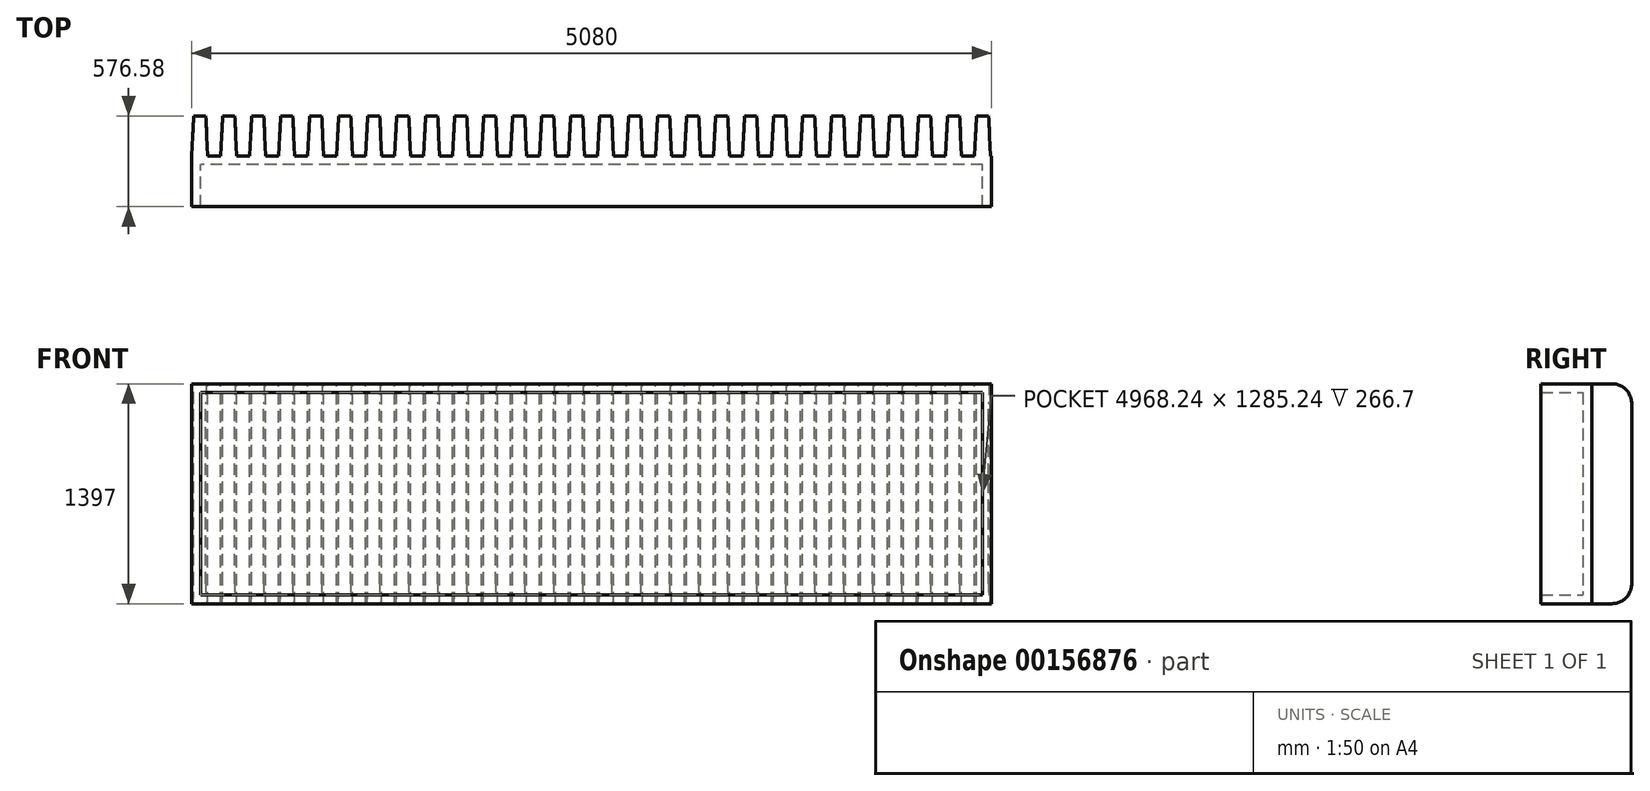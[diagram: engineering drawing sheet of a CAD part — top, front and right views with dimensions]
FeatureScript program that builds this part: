
annotation { "Feature Type Name" : "Feature", "Feature Type Description" : "" }
export const myFeature = defineFeature(function(context is Context, id is Id, definition is map)
    precondition{}
    {
        {
            var Q0;
            Q0=qCreatedBy(makeId("Front.planeOp"),FACE);
            var sketch = newSketch(context, id + "F0", { "sketchPlane" : qUnion([Q0])});
            skLineSegment(sketch, "E0.bottom", {"start": v(2540, 698.5) * mm, "end": v(-2540, 698.5) * mm});
            skLineSegment(sketch, "E0.top", {"start": v(2540, -698.5) * mm, "end": v(-2540, -698.5) * mm});
            skLineSegment(sketch, "E0.left", {"start": v(2540, 698.5) * mm, "end": v(2540, -698.5) * mm});
            skLineSegment(sketch, "E0.right", {"start": v(-2540, 698.5) * mm, "end": v(-2540, -698.5) * mm});
            skPoint(sketch, "E0.middle", {"position": v(0, 0) * mm});
            skSolve(sketch);
        }
        {
            var Q0;
            Q0 = qSketchRegion(id + "F0", true);
            extrude(context, id + "F1", {"entities" : qUnion([Q0]), "depth" : 322.58 * mm});
        }
        {
            var Q0;
            Q0=makeQuery(id+"F1.opExtrude","SWEPT_FACE",FACE,{"disambiguationData":[OSD([sQuery(id+"F0.wireOp",EDGE,"E0.bottom")])]});
            var sketch = newSketch(context, id + "F2", { "sketchPlane" : qUnion([Q0])});
            skLineSegment(sketch, "E1", {"start": v(-2540, 0) * mm, "end": v(-2526.69, 254) * mm});
            skLineSegment(sketch, "E2", {"start": v(-2526.69, 254) * mm, "end": v(-2450.49, 254) * mm});
            skLineSegment(sketch, "E3", {"start": v(-2450.49, 254) * mm, "end": v(-2437.18, 0) * mm});
            skLineSegment(sketch, "E4", {"start": v(-2437.18, 0) * mm, "end": v(-2540, 0) * mm});
            skLineSegment(sketch, "E5.1.0.0", {"start": v(-2266.34, 254) * mm, "end": v(-2253.03, 0) * mm});
            skLineSegment(sketch, "E5.1.0.1", {"start": v(-2342.54, 254) * mm, "end": v(-2266.34, 254) * mm});
            skLineSegment(sketch, "E5.1.0.2", {"start": v(-2355.85, 0) * mm, "end": v(-2342.54, 254) * mm});
            skLineSegment(sketch, "E5.1.0.3", {"start": v(-2253.03, 0) * mm, "end": v(-2355.85, 0) * mm});
            skLineSegment(sketch, "E5.2.0.0", {"start": v(-2082.19, 254) * mm, "end": v(-2068.88, 0) * mm});
            skLineSegment(sketch, "E5.2.0.1", {"start": v(-2158.39, 254) * mm, "end": v(-2082.19, 254) * mm});
            skLineSegment(sketch, "E5.2.0.2", {"start": v(-2171.7, 0) * mm, "end": v(-2158.39, 254) * mm});
            skLineSegment(sketch, "E5.2.0.3", {"start": v(-2068.88, 0) * mm, "end": v(-2171.7, 0) * mm});
            skLineSegment(sketch, "E5.3.0.0", {"start": v(-1898.04, 254) * mm, "end": v(-1884.73, 0) * mm});
            skLineSegment(sketch, "E5.3.0.1", {"start": v(-1974.24, 254) * mm, "end": v(-1898.04, 254) * mm});
            skLineSegment(sketch, "E5.3.0.2", {"start": v(-1987.55, 0) * mm, "end": v(-1974.24, 254) * mm});
            skLineSegment(sketch, "E5.3.0.3", {"start": v(-1884.73, 0) * mm, "end": v(-1987.55, 0) * mm});
            skLineSegment(sketch, "E5.4.0.0", {"start": v(-1713.89, 254) * mm, "end": v(-1700.58, 0) * mm});
            skLineSegment(sketch, "E5.4.0.1", {"start": v(-1790.09, 254) * mm, "end": v(-1713.89, 254) * mm});
            skLineSegment(sketch, "E5.4.0.2", {"start": v(-1803.4, 0) * mm, "end": v(-1790.09, 254) * mm});
            skLineSegment(sketch, "E5.4.0.3", {"start": v(-1700.58, 0) * mm, "end": v(-1803.4, 0) * mm});
            skLineSegment(sketch, "E5.5.0.0", {"start": v(-1529.74, 254) * mm, "end": v(-1516.43, 0) * mm});
            skLineSegment(sketch, "E5.5.0.1", {"start": v(-1605.94, 254) * mm, "end": v(-1529.74, 254) * mm});
            skLineSegment(sketch, "E5.5.0.2", {"start": v(-1619.25, 0) * mm, "end": v(-1605.94, 254) * mm});
            skLineSegment(sketch, "E5.5.0.3", {"start": v(-1516.43, 0) * mm, "end": v(-1619.25, 0) * mm});
            skLineSegment(sketch, "E5.6.0.0", {"start": v(-1345.59, 254) * mm, "end": v(-1332.28, 0) * mm});
            skLineSegment(sketch, "E5.6.0.1", {"start": v(-1421.79, 254) * mm, "end": v(-1345.59, 254) * mm});
            skLineSegment(sketch, "E5.6.0.2", {"start": v(-1435.1, 0) * mm, "end": v(-1421.79, 254) * mm});
            skLineSegment(sketch, "E5.6.0.3", {"start": v(-1332.28, 0) * mm, "end": v(-1435.1, 0) * mm});
            skLineSegment(sketch, "E5.7.0.0", {"start": v(-1161.44, 254) * mm, "end": v(-1148.13, 0) * mm});
            skLineSegment(sketch, "E5.7.0.1", {"start": v(-1237.64, 254) * mm, "end": v(-1161.44, 254) * mm});
            skLineSegment(sketch, "E5.7.0.2", {"start": v(-1250.95, 0) * mm, "end": v(-1237.64, 254) * mm});
            skLineSegment(sketch, "E5.7.0.3", {"start": v(-1148.13, 0) * mm, "end": v(-1250.95, 0) * mm});
            skLineSegment(sketch, "E5.8.0.0", {"start": v(-977.29, 254) * mm, "end": v(-963.98, 0) * mm});
            skLineSegment(sketch, "E5.8.0.1", {"start": v(-1053.49, 254) * mm, "end": v(-977.29, 254) * mm});
            skLineSegment(sketch, "E5.8.0.2", {"start": v(-1066.8, 0) * mm, "end": v(-1053.49, 254) * mm});
            skLineSegment(sketch, "E5.8.0.3", {"start": v(-963.98, 0) * mm, "end": v(-1066.8, 0) * mm});
            skLineSegment(sketch, "E5.9.0.0", {"start": v(-793.14, 254) * mm, "end": v(-779.83, 0) * mm});
            skLineSegment(sketch, "E5.9.0.1", {"start": v(-869.34, 254) * mm, "end": v(-793.14, 254) * mm});
            skLineSegment(sketch, "E5.9.0.2", {"start": v(-882.65, 0) * mm, "end": v(-869.34, 254) * mm});
            skLineSegment(sketch, "E5.9.0.3", {"start": v(-779.83, 0) * mm, "end": v(-882.65, 0) * mm});
            skLineSegment(sketch, "E5.10.0.0", {"start": v(-608.99, 254) * mm, "end": v(-595.68, 0) * mm});
            skLineSegment(sketch, "E5.10.0.1", {"start": v(-685.19, 254) * mm, "end": v(-608.99, 254) * mm});
            skLineSegment(sketch, "E5.10.0.2", {"start": v(-698.5, 0) * mm, "end": v(-685.19, 254) * mm});
            skLineSegment(sketch, "E5.10.0.3", {"start": v(-595.68, 0) * mm, "end": v(-698.5, 0) * mm});
            skLineSegment(sketch, "E5.11.0.0", {"start": v(-424.84, 254) * mm, "end": v(-411.53, 0) * mm});
            skLineSegment(sketch, "E5.11.0.1", {"start": v(-501.04, 254) * mm, "end": v(-424.84, 254) * mm});
            skLineSegment(sketch, "E5.11.0.2", {"start": v(-514.35, 0) * mm, "end": v(-501.04, 254) * mm});
            skLineSegment(sketch, "E5.11.0.3", {"start": v(-411.53, 0) * mm, "end": v(-514.35, 0) * mm});
            skLineSegment(sketch, "E5.12.0.0", {"start": v(-240.69, 254) * mm, "end": v(-227.38, 0) * mm});
            skLineSegment(sketch, "E5.12.0.1", {"start": v(-316.89, 254) * mm, "end": v(-240.69, 254) * mm});
            skLineSegment(sketch, "E5.12.0.2", {"start": v(-330.2, 0) * mm, "end": v(-316.89, 254) * mm});
            skLineSegment(sketch, "E5.12.0.3", {"start": v(-227.38, 0) * mm, "end": v(-330.2, 0) * mm});
            skLineSegment(sketch, "E5.13.0.0", {"start": v(-56.54, 254) * mm, "end": v(-43.23, 0) * mm});
            skLineSegment(sketch, "E5.13.0.1", {"start": v(-132.74, 254) * mm, "end": v(-56.54, 254) * mm});
            skLineSegment(sketch, "E5.13.0.2", {"start": v(-146.05, 0) * mm, "end": v(-132.74, 254) * mm});
            skLineSegment(sketch, "E5.13.0.3", {"start": v(-43.23, 0) * mm, "end": v(-146.05, 0) * mm});
            skLineSegment(sketch, "E5.14.0.0", {"start": v(127.61, 254) * mm, "end": v(140.92, 0) * mm});
            skLineSegment(sketch, "E5.14.0.1", {"start": v(51.41, 254) * mm, "end": v(127.61, 254) * mm});
            skLineSegment(sketch, "E5.14.0.2", {"start": v(38.1, 0) * mm, "end": v(51.41, 254) * mm});
            skLineSegment(sketch, "E5.14.0.3", {"start": v(140.92, 0) * mm, "end": v(38.1, 0) * mm});
            skLineSegment(sketch, "E5.15.0.0", {"start": v(311.76, 254) * mm, "end": v(325.07, 0) * mm});
            skLineSegment(sketch, "E5.15.0.1", {"start": v(235.56, 254) * mm, "end": v(311.76, 254) * mm});
            skLineSegment(sketch, "E5.15.0.2", {"start": v(222.25, 0) * mm, "end": v(235.56, 254) * mm});
            skLineSegment(sketch, "E5.15.0.3", {"start": v(325.07, 0) * mm, "end": v(222.25, 0) * mm});
            skLineSegment(sketch, "E5.16.0.0", {"start": v(495.91, 254) * mm, "end": v(509.22, 0) * mm});
            skLineSegment(sketch, "E5.16.0.1", {"start": v(419.71, 254) * mm, "end": v(495.91, 254) * mm});
            skLineSegment(sketch, "E5.16.0.2", {"start": v(406.4, 0) * mm, "end": v(419.71, 254) * mm});
            skLineSegment(sketch, "E5.16.0.3", {"start": v(509.22, 0) * mm, "end": v(406.4, 0) * mm});
            skLineSegment(sketch, "E5.17.0.0", {"start": v(680.06, 254) * mm, "end": v(693.37, 0) * mm});
            skLineSegment(sketch, "E5.17.0.1", {"start": v(603.86, 254) * mm, "end": v(680.06, 254) * mm});
            skLineSegment(sketch, "E5.17.0.2", {"start": v(590.55, 0) * mm, "end": v(603.86, 254) * mm});
            skLineSegment(sketch, "E5.17.0.3", {"start": v(693.37, 0) * mm, "end": v(590.55, 0) * mm});
            skLineSegment(sketch, "E5.18.0.0", {"start": v(864.21, 254) * mm, "end": v(877.52, 0) * mm});
            skLineSegment(sketch, "E5.18.0.1", {"start": v(788.01, 254) * mm, "end": v(864.21, 254) * mm});
            skLineSegment(sketch, "E5.18.0.2", {"start": v(774.7, 0) * mm, "end": v(788.01, 254) * mm});
            skLineSegment(sketch, "E5.18.0.3", {"start": v(877.52, 0) * mm, "end": v(774.7, 0) * mm});
            skLineSegment(sketch, "E5.19.0.0", {"start": v(1048.36, 254) * mm, "end": v(1061.67, 0) * mm});
            skLineSegment(sketch, "E5.19.0.1", {"start": v(972.16, 254) * mm, "end": v(1048.36, 254) * mm});
            skLineSegment(sketch, "E5.19.0.2", {"start": v(958.85, 0) * mm, "end": v(972.16, 254) * mm});
            skLineSegment(sketch, "E5.19.0.3", {"start": v(1061.67, 0) * mm, "end": v(958.85, 0) * mm});
            skLineSegment(sketch, "E5.20.0.0", {"start": v(1232.51, 254) * mm, "end": v(1245.82, 0) * mm});
            skLineSegment(sketch, "E5.20.0.1", {"start": v(1156.31, 254) * mm, "end": v(1232.51, 254) * mm});
            skLineSegment(sketch, "E5.20.0.2", {"start": v(1143, 0) * mm, "end": v(1156.31, 254) * mm});
            skLineSegment(sketch, "E5.20.0.3", {"start": v(1245.82, 0) * mm, "end": v(1143, 0) * mm});
            skLineSegment(sketch, "E5.21.0.0", {"start": v(1416.66, 254) * mm, "end": v(1429.97, 0) * mm});
            skLineSegment(sketch, "E5.21.0.1", {"start": v(1340.46, 254) * mm, "end": v(1416.66, 254) * mm});
            skLineSegment(sketch, "E5.21.0.2", {"start": v(1327.15, 0) * mm, "end": v(1340.46, 254) * mm});
            skLineSegment(sketch, "E5.21.0.3", {"start": v(1429.97, 0) * mm, "end": v(1327.15, 0) * mm});
            skLineSegment(sketch, "E5.22.0.0", {"start": v(1600.81, 254) * mm, "end": v(1614.12, 0) * mm});
            skLineSegment(sketch, "E5.22.0.1", {"start": v(1524.61, 254) * mm, "end": v(1600.81, 254) * mm});
            skLineSegment(sketch, "E5.22.0.2", {"start": v(1511.3, 0) * mm, "end": v(1524.61, 254) * mm});
            skLineSegment(sketch, "E5.22.0.3", {"start": v(1614.12, 0) * mm, "end": v(1511.3, 0) * mm});
            skLineSegment(sketch, "E5.23.0.0", {"start": v(1784.96, 254) * mm, "end": v(1798.27, 0) * mm});
            skLineSegment(sketch, "E5.23.0.1", {"start": v(1708.76, 254) * mm, "end": v(1784.96, 254) * mm});
            skLineSegment(sketch, "E5.23.0.2", {"start": v(1695.45, 0) * mm, "end": v(1708.76, 254) * mm});
            skLineSegment(sketch, "E5.23.0.3", {"start": v(1798.27, 0) * mm, "end": v(1695.45, 0) * mm});
            skLineSegment(sketch, "E5.24.0.0", {"start": v(1969.11, 254) * mm, "end": v(1982.42, 0) * mm});
            skLineSegment(sketch, "E5.24.0.1", {"start": v(1892.91, 254) * mm, "end": v(1969.11, 254) * mm});
            skLineSegment(sketch, "E5.24.0.2", {"start": v(1879.6, 0) * mm, "end": v(1892.91, 254) * mm});
            skLineSegment(sketch, "E5.24.0.3", {"start": v(1982.42, 0) * mm, "end": v(1879.6, 0) * mm});
            skLineSegment(sketch, "E5.25.0.0", {"start": v(2153.26, 254) * mm, "end": v(2166.57, 0) * mm});
            skLineSegment(sketch, "E5.25.0.1", {"start": v(2077.06, 254) * mm, "end": v(2153.26, 254) * mm});
            skLineSegment(sketch, "E5.25.0.2", {"start": v(2063.75, 0) * mm, "end": v(2077.06, 254) * mm});
            skLineSegment(sketch, "E5.25.0.3", {"start": v(2166.57, 0) * mm, "end": v(2063.75, 0) * mm});
            skLineSegment(sketch, "E5.26.0.0", {"start": v(2337.41, 254) * mm, "end": v(2350.72, 0) * mm});
            skLineSegment(sketch, "E5.26.0.1", {"start": v(2261.21, 254) * mm, "end": v(2337.41, 254) * mm});
            skLineSegment(sketch, "E5.26.0.2", {"start": v(2247.9, 0) * mm, "end": v(2261.21, 254) * mm});
            skLineSegment(sketch, "E5.26.0.3", {"start": v(2350.72, 0) * mm, "end": v(2247.9, 0) * mm});
            skLineSegment(sketch, "E5.27.0.0", {"start": v(2521.56, 254) * mm, "end": v(2534.87, 0) * mm});
            skLineSegment(sketch, "E5.27.0.1", {"start": v(2445.36, 254) * mm, "end": v(2521.56, 254) * mm});
            skLineSegment(sketch, "E5.27.0.2", {"start": v(2432.05, 0) * mm, "end": v(2445.36, 254) * mm});
            skLineSegment(sketch, "E5.27.0.3", {"start": v(2534.87, 0) * mm, "end": v(2432.05, 0) * mm});
            skLineSegment(sketch, "E5.direction1", {"start": v(-2437.18, 0) * mm, "end": v(-2253.03, 0) * mm, "construction": true});
            skSolve(sketch);
        }
        {
            var Q0;
            Q0 = qSketchRegion(id + "F2", true);
            extrude(context, id + "F3", {"entities" : qUnion([Q0]), "operationType" : NewBodyOperationType.ADD, "oppositeDirection" : true, "depth" : 1397 * mm});
        }
        {
            var Q0;
            Q0=makeQuery(id+"F1.opExtrude","CAP_FACE",FACE,{"disambiguationData":[OSD([sQuery(id+"F0.wireOp",EDGE,"E0.bottom"),sQuery(id+"F0.wireOp",EDGE,"E0.top"),sQuery(id+"F0.wireOp",EDGE,"E0.left"),sQuery(id+"F0.wireOp",EDGE,"E0.right")])],"isStart":false});
            shell(context, id + "F4", {"entities" : qUnion([Q0]), "thickness" : 55.88 * mm});
        }
        {
            var Q0;
            Q0=makeQuery(id+"F3.opExtrude","CAP_EDGE",EDGE,{"disambiguationData":[OSD([sQuery(id+"F2.wireOp",EDGE,"E2")])],"isStart":true});
            var Q1;
            Q1=makeQuery(id+"F3.opExtrude","CAP_EDGE",EDGE,{"disambiguationData":[OSD([sQuery(id+"F2.wireOp",EDGE,"E5.1.0.1")])],"isStart":true});
            var Q2;
            Q2=makeQuery(id+"F3.opExtrude","CAP_EDGE",EDGE,{"disambiguationData":[OSD([sQuery(id+"F2.wireOp",EDGE,"E5.2.0.1")])],"isStart":true});
            var Q3;
            Q3=makeQuery(id+"F3.opExtrude","CAP_EDGE",EDGE,{"disambiguationData":[OSD([sQuery(id+"F2.wireOp",EDGE,"E5.3.0.1")])],"isStart":true});
            var Q4;
            Q4=makeQuery(id+"F3.opExtrude","CAP_EDGE",EDGE,{"disambiguationData":[OSD([sQuery(id+"F2.wireOp",EDGE,"E5.4.0.1")])],"isStart":true});
            var Q5;
            Q5=makeQuery(id+"F3.opExtrude","CAP_EDGE",EDGE,{"disambiguationData":[OSD([sQuery(id+"F2.wireOp",EDGE,"E5.5.0.1")])],"isStart":true});
            var Q6;
            Q6=makeQuery(id+"F3.opExtrude","CAP_EDGE",EDGE,{"disambiguationData":[OSD([sQuery(id+"F2.wireOp",EDGE,"E5.6.0.1")])],"isStart":true});
            var Q7;
            Q7=makeQuery(id+"F3.opExtrude","CAP_EDGE",EDGE,{"disambiguationData":[OSD([sQuery(id+"F2.wireOp",EDGE,"E5.7.0.1")])],"isStart":true});
            var Q8;
            Q8=makeQuery(id+"F3.opExtrude","CAP_EDGE",EDGE,{"disambiguationData":[OSD([sQuery(id+"F2.wireOp",EDGE,"E5.8.0.1")])],"isStart":true});
            var Q9;
            Q9=makeQuery(id+"F3.opExtrude","CAP_EDGE",EDGE,{"disambiguationData":[OSD([sQuery(id+"F2.wireOp",EDGE,"E5.9.0.1")])],"isStart":true});
            var Q10;
            Q10=makeQuery(id+"F3.opExtrude","CAP_EDGE",EDGE,{"disambiguationData":[OSD([sQuery(id+"F2.wireOp",EDGE,"E5.10.0.1")])],"isStart":true});
            var Q11;
            Q11=makeQuery(id+"F3.opExtrude","CAP_EDGE",EDGE,{"disambiguationData":[OSD([sQuery(id+"F2.wireOp",EDGE,"E5.11.0.1")])],"isStart":true});
            var Q12;
            Q12=makeQuery(id+"F3.opExtrude","CAP_EDGE",EDGE,{"disambiguationData":[OSD([sQuery(id+"F2.wireOp",EDGE,"E5.12.0.1")])],"isStart":true});
            var Q13;
            Q13=makeQuery(id+"F3.opExtrude","CAP_EDGE",EDGE,{"disambiguationData":[OSD([sQuery(id+"F2.wireOp",EDGE,"E5.13.0.1")])],"isStart":true});
            var Q14;
            Q14=makeQuery(id+"F3.opExtrude","CAP_EDGE",EDGE,{"disambiguationData":[OSD([sQuery(id+"F2.wireOp",EDGE,"E5.14.0.1")])],"isStart":true});
            var Q15;
            Q15=makeQuery(id+"F3.opExtrude","CAP_EDGE",EDGE,{"disambiguationData":[OSD([sQuery(id+"F2.wireOp",EDGE,"E5.15.0.1")])],"isStart":true});
            var Q16;
            Q16=makeQuery(id+"F3.opExtrude","CAP_EDGE",EDGE,{"disambiguationData":[OSD([sQuery(id+"F2.wireOp",EDGE,"E5.16.0.1")])],"isStart":true});
            var Q17;
            Q17=makeQuery(id+"F3.opExtrude","CAP_EDGE",EDGE,{"disambiguationData":[OSD([sQuery(id+"F2.wireOp",EDGE,"E5.17.0.1")])],"isStart":true});
            var Q18;
            Q18=makeQuery(id+"F3.opExtrude","CAP_EDGE",EDGE,{"disambiguationData":[OSD([sQuery(id+"F2.wireOp",EDGE,"E5.18.0.1")])],"isStart":true});
            var Q19;
            Q19=makeQuery(id+"F3.opExtrude","CAP_EDGE",EDGE,{"disambiguationData":[OSD([sQuery(id+"F2.wireOp",EDGE,"E5.19.0.1")])],"isStart":true});
            var Q20;
            Q20=makeQuery(id+"F3.opExtrude","CAP_EDGE",EDGE,{"disambiguationData":[OSD([sQuery(id+"F2.wireOp",EDGE,"E5.20.0.1")])],"isStart":true});
            var Q21;
            Q21=makeQuery(id+"F3.opExtrude","CAP_EDGE",EDGE,{"disambiguationData":[OSD([sQuery(id+"F2.wireOp",EDGE,"E5.21.0.1")])],"isStart":true});
            var Q22;
            Q22=makeQuery(id+"F3.opExtrude","CAP_EDGE",EDGE,{"disambiguationData":[OSD([sQuery(id+"F2.wireOp",EDGE,"E5.22.0.1")])],"isStart":true});
            var Q23;
            Q23=makeQuery(id+"F3.opExtrude","CAP_EDGE",EDGE,{"disambiguationData":[OSD([sQuery(id+"F2.wireOp",EDGE,"E5.23.0.1")])],"isStart":true});
            var Q24;
            Q24=makeQuery(id+"F3.opExtrude","CAP_EDGE",EDGE,{"disambiguationData":[OSD([sQuery(id+"F2.wireOp",EDGE,"E5.24.0.1")])],"isStart":true});
            var Q25;
            Q25=makeQuery(id+"F3.opExtrude","CAP_EDGE",EDGE,{"disambiguationData":[OSD([sQuery(id+"F2.wireOp",EDGE,"E5.25.0.1")])],"isStart":true});
            var Q26;
            Q26=makeQuery(id+"F3.opExtrude","CAP_EDGE",EDGE,{"disambiguationData":[OSD([sQuery(id+"F2.wireOp",EDGE,"E5.26.0.1")])],"isStart":true});
            var Q27;
            Q27=makeQuery(id+"F3.opExtrude","CAP_EDGE",EDGE,{"disambiguationData":[OSD([sQuery(id+"F2.wireOp",EDGE,"E5.27.0.1")])],"isStart":true});
            var Q28;
            Q28=makeQuery(id+"F3.opExtrude","CAP_EDGE",EDGE,{"disambiguationData":[OSD([sQuery(id+"F2.wireOp",EDGE,"E2")])],"isStart":false});
            var Q29;
            Q29=makeQuery(id+"F3.opExtrude","CAP_EDGE",EDGE,{"disambiguationData":[OSD([sQuery(id+"F2.wireOp",EDGE,"E5.1.0.1")])],"isStart":false});
            var Q30;
            Q30=makeQuery(id+"F3.opExtrude","CAP_EDGE",EDGE,{"disambiguationData":[OSD([sQuery(id+"F2.wireOp",EDGE,"E5.2.0.1")])],"isStart":false});
            var Q31;
            Q31=makeQuery(id+"F3.opExtrude","CAP_EDGE",EDGE,{"disambiguationData":[OSD([sQuery(id+"F2.wireOp",EDGE,"E5.3.0.1")])],"isStart":false});
            var Q32;
            Q32=makeQuery(id+"F3.opExtrude","CAP_EDGE",EDGE,{"disambiguationData":[OSD([sQuery(id+"F2.wireOp",EDGE,"E5.4.0.1")])],"isStart":false});
            var Q33;
            Q33=makeQuery(id+"F3.opExtrude","CAP_EDGE",EDGE,{"disambiguationData":[OSD([sQuery(id+"F2.wireOp",EDGE,"E5.5.0.1")])],"isStart":false});
            var Q34;
            Q34=makeQuery(id+"F3.opExtrude","CAP_EDGE",EDGE,{"disambiguationData":[OSD([sQuery(id+"F2.wireOp",EDGE,"E5.6.0.1")])],"isStart":false});
            var Q35;
            Q35=makeQuery(id+"F3.opExtrude","CAP_EDGE",EDGE,{"disambiguationData":[OSD([sQuery(id+"F2.wireOp",EDGE,"E5.7.0.1")])],"isStart":false});
            var Q36;
            Q36=makeQuery(id+"F3.opExtrude","CAP_EDGE",EDGE,{"disambiguationData":[OSD([sQuery(id+"F2.wireOp",EDGE,"E5.8.0.1")])],"isStart":false});
            var Q37;
            Q37=makeQuery(id+"F3.opExtrude","CAP_EDGE",EDGE,{"disambiguationData":[OSD([sQuery(id+"F2.wireOp",EDGE,"E5.9.0.1")])],"isStart":false});
            var Q38;
            Q38=makeQuery(id+"F3.opExtrude","CAP_EDGE",EDGE,{"disambiguationData":[OSD([sQuery(id+"F2.wireOp",EDGE,"E5.10.0.1")])],"isStart":false});
            var Q39;
            Q39=makeQuery(id+"F3.opExtrude","CAP_EDGE",EDGE,{"disambiguationData":[OSD([sQuery(id+"F2.wireOp",EDGE,"E5.11.0.1")])],"isStart":false});
            var Q40;
            Q40=makeQuery(id+"F3.opExtrude","CAP_EDGE",EDGE,{"disambiguationData":[OSD([sQuery(id+"F2.wireOp",EDGE,"E5.12.0.1")])],"isStart":false});
            var Q41;
            Q41=makeQuery(id+"F3.opExtrude","CAP_EDGE",EDGE,{"disambiguationData":[OSD([sQuery(id+"F2.wireOp",EDGE,"E5.13.0.1")])],"isStart":false});
            var Q42;
            Q42=makeQuery(id+"F3.opExtrude","CAP_EDGE",EDGE,{"disambiguationData":[OSD([sQuery(id+"F2.wireOp",EDGE,"E5.14.0.1")])],"isStart":false});
            var Q43;
            Q43=makeQuery(id+"F3.opExtrude","CAP_EDGE",EDGE,{"disambiguationData":[OSD([sQuery(id+"F2.wireOp",EDGE,"E5.15.0.1")])],"isStart":false});
            var Q44;
            Q44=makeQuery(id+"F3.opExtrude","CAP_EDGE",EDGE,{"disambiguationData":[OSD([sQuery(id+"F2.wireOp",EDGE,"E5.16.0.1")])],"isStart":false});
            var Q45;
            Q45=makeQuery(id+"F3.opExtrude","CAP_EDGE",EDGE,{"disambiguationData":[OSD([sQuery(id+"F2.wireOp",EDGE,"E5.17.0.1")])],"isStart":false});
            var Q46;
            Q46=makeQuery(id+"F3.opExtrude","CAP_EDGE",EDGE,{"disambiguationData":[OSD([sQuery(id+"F2.wireOp",EDGE,"E5.18.0.1")])],"isStart":false});
            var Q47;
            Q47=makeQuery(id+"F3.opExtrude","CAP_EDGE",EDGE,{"disambiguationData":[OSD([sQuery(id+"F2.wireOp",EDGE,"E5.19.0.1")])],"isStart":false});
            var Q48;
            Q48=makeQuery(id+"F3.opExtrude","CAP_EDGE",EDGE,{"disambiguationData":[OSD([sQuery(id+"F2.wireOp",EDGE,"E5.20.0.1")])],"isStart":false});
            var Q49;
            Q49=makeQuery(id+"F3.opExtrude","CAP_EDGE",EDGE,{"disambiguationData":[OSD([sQuery(id+"F2.wireOp",EDGE,"E5.21.0.1")])],"isStart":false});
            var Q50;
            Q50=makeQuery(id+"F3.opExtrude","CAP_EDGE",EDGE,{"disambiguationData":[OSD([sQuery(id+"F2.wireOp",EDGE,"E5.22.0.1")])],"isStart":false});
            var Q51;
            Q51=makeQuery(id+"F3.opExtrude","CAP_EDGE",EDGE,{"disambiguationData":[OSD([sQuery(id+"F2.wireOp",EDGE,"E5.23.0.1")])],"isStart":false});
            var Q52;
            Q52=makeQuery(id+"F3.opExtrude","CAP_EDGE",EDGE,{"disambiguationData":[OSD([sQuery(id+"F2.wireOp",EDGE,"E5.24.0.1")])],"isStart":false});
            var Q53;
            Q53=makeQuery(id+"F3.opExtrude","CAP_EDGE",EDGE,{"disambiguationData":[OSD([sQuery(id+"F2.wireOp",EDGE,"E5.25.0.1")])],"isStart":false});
            var Q54;
            Q54=makeQuery(id+"F3.opExtrude","CAP_EDGE",EDGE,{"disambiguationData":[OSD([sQuery(id+"F2.wireOp",EDGE,"E5.26.0.1")])],"isStart":false});
            var Q55;
            Q55=makeQuery(id+"F3.opExtrude","CAP_EDGE",EDGE,{"disambiguationData":[OSD([sQuery(id+"F2.wireOp",EDGE,"E5.27.0.1")])],"isStart":false});
            fillet(context, id + "F5", {"entities" : qUnion([Q0, Q1, Q2, Q3, Q4, Q5, Q6, Q7, Q8, Q9, Q10, Q11, Q12, Q13, Q14, Q15, Q16, Q17, Q18, Q19, Q20, Q21, Q22, Q23, Q24, Q25, Q26, Q27, Q28, Q29, Q30, Q31, Q32, Q33, Q34, Q35, Q36, Q37, Q38, Q39, Q40, Q41, Q42, Q43, Q44, Q45, Q46, Q47, Q48, Q49, Q50, Q51, Q52, Q53, Q54, Q55]), "radius" : 127 * mm, "tangentPropagation" : true, "allowEdgeOverflow" : false});
        }
    });
